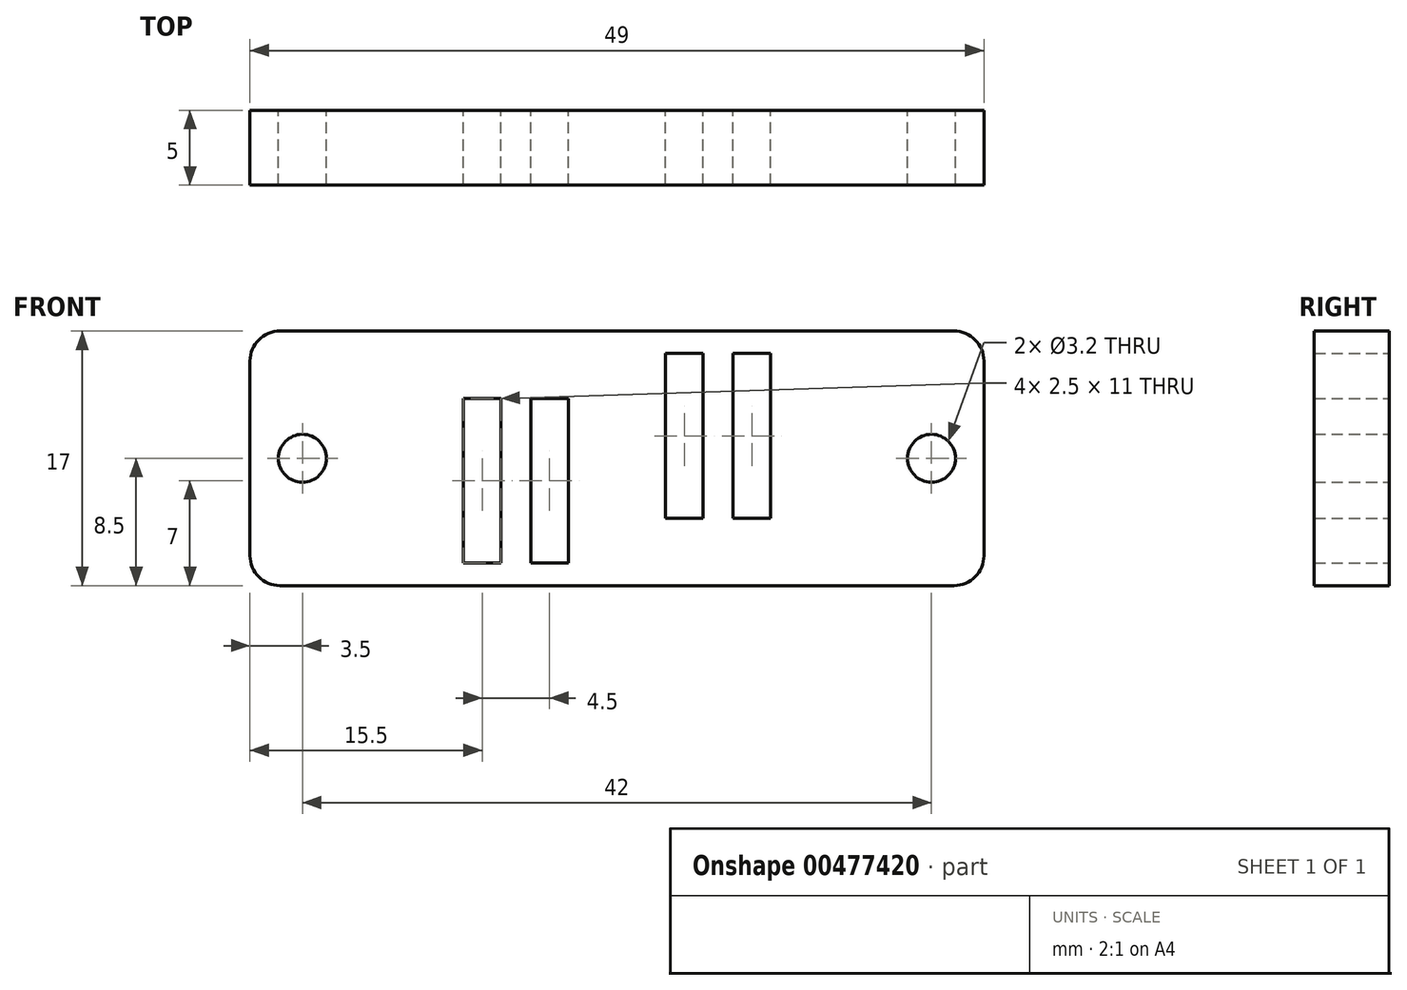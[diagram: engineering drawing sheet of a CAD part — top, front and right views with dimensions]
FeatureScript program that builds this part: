
annotation { "Feature Type Name" : "Feature", "Feature Type Description" : "" }
export const myFeature = defineFeature(function(context is Context, id is Id, definition is map)
    precondition{}
    {
        {
            var Q0;
            Q0=qCreatedBy(makeId("Front.planeOp"),FACE);
            var sketch = newSketch(context, id + "F0", { "sketchPlane" : qUnion([Q0])});
            skLineSegment(sketch, "E0.bottom", {"start": v(-24.5, -8.5) * mm, "end": v(24.5, -8.5) * mm});
            skLineSegment(sketch, "E0.top", {"start": v(-24.5, 8.5) * mm, "end": v(24.5, 8.5) * mm});
            skLineSegment(sketch, "E0.left", {"start": v(-24.5, -8.5) * mm, "end": v(-24.5, 8.5) * mm});
            skLineSegment(sketch, "E0.right", {"start": v(24.5, -8.5) * mm, "end": v(24.5, 8.5) * mm});
            skPoint(sketch, "E0.middle", {"position": v(0, 0) * mm});
            skPoint(sketch, "E1", {"position": v(-21, 0) * mm});
            skPoint(sketch, "E2", {"position": v(21, 0) * mm});
            skLineSegment(sketch, "E3.bottom", {"start": v(7.75, -4) * mm, "end": v(10.25, -4) * mm});
            skLineSegment(sketch, "E3.top", {"start": v(7.75, 7) * mm, "end": v(10.25, 7) * mm});
            skLineSegment(sketch, "E3.left", {"start": v(7.75, -4) * mm, "end": v(7.75, 7) * mm});
            skLineSegment(sketch, "E3.right", {"start": v(10.25, -4) * mm, "end": v(10.25, 7) * mm});
            skPoint(sketch, "E3.middle", {"position": v(9, 1.5) * mm});
            skLineSegment(sketch, "E4.bottom", {"start": v(3.25, -4) * mm, "end": v(5.75, -4) * mm});
            skLineSegment(sketch, "E4.top", {"start": v(3.25, 7) * mm, "end": v(5.75, 7) * mm});
            skLineSegment(sketch, "E4.left", {"start": v(3.25, -4) * mm, "end": v(3.25, 7) * mm});
            skLineSegment(sketch, "E4.right", {"start": v(5.75, -4) * mm, "end": v(5.75, 7) * mm});
            skPoint(sketch, "E4.middle", {"position": v(4.5, 1.5) * mm});
            skLineSegment(sketch, "E5.bottom", {"start": v(-5.75, -7) * mm, "end": v(-3.25, -7) * mm});
            skLineSegment(sketch, "E5.top", {"start": v(-5.75, 4) * mm, "end": v(-3.25, 4) * mm});
            skLineSegment(sketch, "E5.left", {"start": v(-5.75, -7) * mm, "end": v(-5.75, 4) * mm});
            skLineSegment(sketch, "E5.right", {"start": v(-3.25, -7) * mm, "end": v(-3.25, 4) * mm});
            skPoint(sketch, "E5.middle", {"position": v(-4.5, -1.5) * mm});
            skLineSegment(sketch, "E6.bottom", {"start": v(-10.25, -7) * mm, "end": v(-7.75, -7) * mm});
            skLineSegment(sketch, "E6.top", {"start": v(-10.25, 4) * mm, "end": v(-7.75, 4) * mm});
            skLineSegment(sketch, "E6.left", {"start": v(-10.25, -7) * mm, "end": v(-10.25, 4) * mm});
            skLineSegment(sketch, "E6.right", {"start": v(-7.75, -7) * mm, "end": v(-7.75, 4) * mm});
            skPoint(sketch, "E6.middle", {"position": v(-9, -1.5) * mm});
            skSolve(sketch);
        }
        {
            var Q0;
            Q0=makeQuery(id+"F0.imprint","IMPRINT",FACE,{"disambiguationData":[TD([[makeQuery(id+"F0.imprint","IMPRINT",EDGE,{"derivedFrom":sQuery(id+"F0.wireOp",EDGE,"E0.bottom")}),1.0]])]});
            extrude(context, id + "F1", {"entities" : qUnion([Q0]), "depth" : 5 * mm});
        }
        {
            var Q0;
            Q0=qCreatedBy(makeId("Front.planeOp"),FACE);
            var sketch = newSketch(context, id + "F2", { "sketchPlane" : qUnion([Q0])});
            skPoint(sketch, "E7", {"position": v(-21, 0) * mm});
            skPoint(sketch, "E8", {"position": v(21, 0) * mm});
            skSolve(sketch);
        }
        {
            var Q0;
            Q0=sQuery(id+"F2.wireOp",VERTEX,"E7");
            var Q1;
            Q1=sQuery(id+"F2.wireOp",VERTEX,"E8");
            var Q2;
            Q2=makeQuery(id+"F1.opExtrude","SWEPT_BODY",BODY,{"disambiguationData":[OSD([sQuery(id+"F0.wireOp",EDGE,"E0.bottom"),sQuery(id+"F0.wireOp",EDGE,"E0.top"),sQuery(id+"F0.wireOp",EDGE,"E0.left"),sQuery(id+"F0.wireOp",EDGE,"E0.right"),sQuery(id+"F0.wireOp",EDGE,"E3.bottom"),sQuery(id+"F0.wireOp",EDGE,"E3.top"),sQuery(id+"F0.wireOp",EDGE,"E3.left"),sQuery(id+"F0.wireOp",EDGE,"E3.right"),sQuery(id+"F0.wireOp",EDGE,"E4.bottom"),sQuery(id+"F0.wireOp",EDGE,"E4.top"),sQuery(id+"F0.wireOp",EDGE,"E4.left"),sQuery(id+"F0.wireOp",EDGE,"E4.right"),sQuery(id+"F0.wireOp",EDGE,"E5.bottom"),sQuery(id+"F0.wireOp",EDGE,"E5.top"),sQuery(id+"F0.wireOp",EDGE,"E5.left"),sQuery(id+"F0.wireOp",EDGE,"E5.right"),sQuery(id+"F0.wireOp",EDGE,"E6.bottom"),sQuery(id+"F0.wireOp",EDGE,"E6.top"),sQuery(id+"F0.wireOp",EDGE,"E6.left"),sQuery(id+"F0.wireOp",EDGE,"E6.right")])]});
            hole(context, id + "F3", {"style" : HoleStyle.SIMPLE, "endStyle" : HoleEndStyle.THROUGH, "oppositeDirection" : true, "holeDiameter" : 3.2 * mm, "isTappedThrough" : true, "tappedDepth" : 12 * mm, "tapClearance" : 3, "locations" : qUnion([Q0, Q1]), "scope" : qUnion([Q2])});
        }
        {
            var Q0;
            Q0=makeQuery(id+"F1.opExtrude","SWEPT_EDGE",EDGE,{"disambiguationData":[OSD([sQuery(id+"F0.wireOp",EDGE,"E0.top"),sQuery(id+"F0.wireOp",EDGE,"E0.left")])]});
            var Q1;
            Q1=makeQuery(id+"F1.opExtrude","SWEPT_EDGE",EDGE,{"disambiguationData":[OSD([sQuery(id+"F0.wireOp",EDGE,"E0.bottom"),sQuery(id+"F0.wireOp",EDGE,"E0.left")])]});
            var Q2;
            Q2=makeQuery(id+"F1.opExtrude","SWEPT_EDGE",EDGE,{"disambiguationData":[OSD([sQuery(id+"F0.wireOp",EDGE,"E0.top"),sQuery(id+"F0.wireOp",EDGE,"E0.right")])]});
            var Q3;
            Q3=makeQuery(id+"F1.opExtrude","SWEPT_EDGE",EDGE,{"disambiguationData":[OSD([sQuery(id+"F0.wireOp",EDGE,"E0.bottom"),sQuery(id+"F0.wireOp",EDGE,"E0.right")])]});
            fillet(context, id + "F4", {"entities" : qUnion([Q0, Q1, Q2, Q3]), "radius" : 2 * mm, "tangentPropagation" : true, "allowEdgeOverflow" : false});
        }
    });
